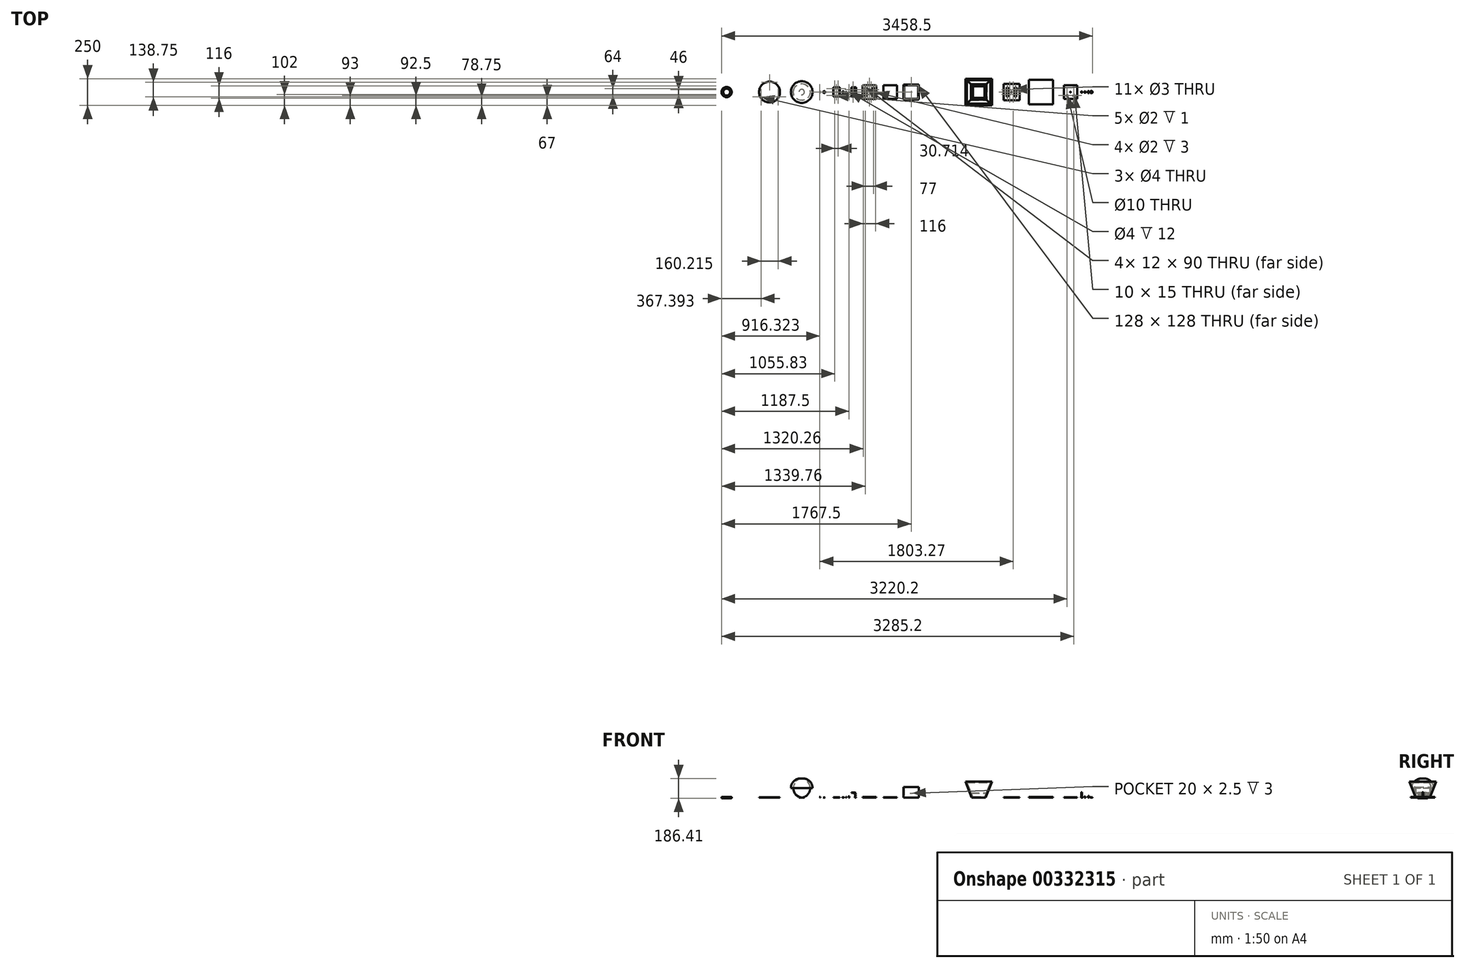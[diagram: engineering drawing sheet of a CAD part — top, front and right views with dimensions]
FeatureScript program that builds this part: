
annotation { "Feature Type Name" : "Feature", "Feature Type Description" : "" }
export const myFeature = defineFeature(function(context is Context, id is Id, definition is map)
    precondition{}
    {
        {
            var Q0;
            Q0=qCreatedBy(makeId("Top.planeOp"),FACE);
            var sketch = newSketch(context, id + "F0", { "sketchPlane" : qUnion([Q0])});
            skLineSegment(sketch, "E0.bottom", {"start": v(-350, -70) * mm, "end": v(-210, -70) * mm});
            skLineSegment(sketch, "E0.top", {"start": v(-350, 70) * mm, "end": v(-210, 70) * mm});
            skLineSegment(sketch, "E0.left", {"start": v(-350, -70) * mm, "end": v(-350, 70) * mm});
            skLineSegment(sketch, "E0.right", {"start": v(-210, -70) * mm, "end": v(-210, 70) * mm});
            skPoint(sketch, "E0.middle", {"position": v(-280, 0) * mm});
            skLineSegment(sketch, "E1.bottom", {"start": v(-344, -64) * mm, "end": v(-216, -64) * mm});
            skLineSegment(sketch, "E1.top", {"start": v(-344, 64) * mm, "end": v(-216, 64) * mm});
            skLineSegment(sketch, "E1.left", {"start": v(-344, -64) * mm, "end": v(-344, 64) * mm});
            skLineSegment(sketch, "E1.right", {"start": v(-216, -64) * mm, "end": v(-216, 64) * mm});
            skSolve(sketch);
        }
        {
            var Q0;
            Q0 = qSketchRegion(id + "F0", true);
            extrude(context, id + "F1", {"entities" : qUnion([Q0]), "depth" : 100 * mm});
        }
        {
            var Q0;
            Q0=qCreatedBy(makeId("Top.planeOp"),FACE);
            var sketch = newSketch(context, id + "F2", { "sketchPlane" : qUnion([Q0])});
            skLineSegment(sketch, "E2.bottom", {"start": v(-539.54, -64) * mm, "end": v(-411.54, -64) * mm});
            skLineSegment(sketch, "E2.top", {"start": v(-539.54, 64) * mm, "end": v(-411.54, 64) * mm});
            skLineSegment(sketch, "E2.left", {"start": v(-539.54, -64) * mm, "end": v(-539.54, 64) * mm});
            skLineSegment(sketch, "E2.right", {"start": v(-411.54, -64) * mm, "end": v(-411.54, 64) * mm});
            skPoint(sketch, "E2.middle", {"position": v(-475.54, 0) * mm});
            skSolve(sketch);
        }
        {
            var Q0;
            Q0 = qSketchRegion(id + "F2", true);
            extrude(context, id + "F3", {"entities" : qUnion([Q0]), "depth" : 4 * mm});
        }
        {
            var Q0;
            Q0=qCreatedBy(makeId("Top.planeOp"),FACE);
            var sketch = newSketch(context, id + "F4", { "sketchPlane" : qUnion([Q0])});
            skLineSegment(sketch, "E3.bottom", {"start": v(-733.24, -64) * mm, "end": v(-605.24, -64) * mm});
            skLineSegment(sketch, "E3.top", {"start": v(-733.24, 64) * mm, "end": v(-605.24, 64) * mm});
            skLineSegment(sketch, "E3.left", {"start": v(-733.24, -64) * mm, "end": v(-733.24, 64) * mm});
            skLineSegment(sketch, "E3.right", {"start": v(-605.24, -64) * mm, "end": v(-605.24, 64) * mm});
            skPoint(sketch, "E3.middle", {"position": v(-669.24, 0) * mm});
            skSolve(sketch);
        }
        {
            var Q0;
            Q0 = qSketchRegion(id + "F4", true);
            extrude(context, id + "F5", {"entities" : qUnion([Q0]), "depth" : 6 * mm});
        }
        {
            var Q0;
            Q0=makeQuery(id+"F5.opExtrude","CAP_FACE",FACE,{"disambiguationData":[OSD([sQuery(id+"F4.wireOp",EDGE,"E3.bottom"),sQuery(id+"F4.wireOp",EDGE,"E3.top"),sQuery(id+"F4.wireOp",EDGE,"E3.left"),sQuery(id+"F4.wireOp",EDGE,"E3.right")])],"isStart":false});
            var sketch = newSketch(context, id + "F6", { "sketchPlane" : qUnion([Q0])});
            skLineSegment(sketch, "E4.bottom", {"start": v(-713.74, 45) * mm, "end": v(-701.74, 45) * mm});
            skLineSegment(sketch, "E4.top", {"start": v(-713.74, -45) * mm, "end": v(-701.74, -45) * mm});
            skLineSegment(sketch, "E4.left", {"start": v(-713.74, 45) * mm, "end": v(-713.74, -45) * mm});
            skLineSegment(sketch, "E4.right", {"start": v(-701.74, 45) * mm, "end": v(-701.74, -45) * mm});
            skLineSegment(sketch, "E5.bottom", {"start": v(-636.74, 45) * mm, "end": v(-624.74, 45) * mm});
            skLineSegment(sketch, "E5.top", {"start": v(-636.74, -45) * mm, "end": v(-624.74, -45) * mm});
            skLineSegment(sketch, "E5.left", {"start": v(-636.74, 45) * mm, "end": v(-636.74, -45) * mm});
            skLineSegment(sketch, "E5.right", {"start": v(-624.74, 45) * mm, "end": v(-624.74, -45) * mm});
            skSolve(sketch);
        }
        {
            var Q0;
            Q0 = qSketchRegion(id + "F6", true);
            extrude(context, id + "F7", {"entities" : qUnion([Q0]), "operationType" : NewBodyOperationType.REMOVE, "oppositeDirection" : true, "depth" : 6 * mm});
        }
        {
            var Q0;
            Q0=qCreatedBy(makeId("Front.planeOp"),FACE);
            var sketch = newSketch(context, id + "F8", { "sketchPlane" : qUnion([Q0])});
            skLineSegment(sketch, "E6", {"start": v(-794.34, 0) * mm, "end": v(-805.34, 0) * mm});
            skLineSegment(sketch, "E7", {"start": v(-805.34, 0) * mm, "end": v(-805.34, 2) * mm});
            skLineSegment(sketch, "E8", {"start": v(-805.34, 2) * mm, "end": v(-803.34, 2) * mm});
            skLineSegment(sketch, "E9", {"start": v(-803.34, 2) * mm, "end": v(-803.34, 4.5) * mm});
            skLineSegment(sketch, "E10", {"start": v(-803.34, 4.5) * mm, "end": v(-805.34, 4.5) * mm});
            skLineSegment(sketch, "E11", {"start": v(-805.34, 4.5) * mm, "end": v(-805.34, 5.5) * mm});
            skLineSegment(sketch, "E12", {"start": v(-805.34, 5.5) * mm, "end": v(-803.34, 5.5) * mm});
            skLineSegment(sketch, "E13", {"start": v(-803.34, 5.5) * mm, "end": v(-803.34, 8) * mm});
            skLineSegment(sketch, "E14", {"start": v(-803.34, 8) * mm, "end": v(-805.34, 8) * mm});
            skLineSegment(sketch, "E15", {"start": v(-805.34, 8) * mm, "end": v(-805.34, 9) * mm});
            skLineSegment(sketch, "E16", {"start": v(-805.34, 9) * mm, "end": v(-803.34, 9) * mm});
            skLineSegment(sketch, "E17", {"start": v(-803.34, 9) * mm, "end": v(-803.34, 11.5) * mm});
            skLineSegment(sketch, "E18", {"start": v(-803.34, 11.5) * mm, "end": v(-805.34, 11.5) * mm});
            skLineSegment(sketch, "E19", {"start": v(-805.34, 11.5) * mm, "end": v(-805.34, 12.5) * mm});
            skLineSegment(sketch, "E20", {"start": v(-805.34, 12.5) * mm, "end": v(-803.34, 12.5) * mm});
            skLineSegment(sketch, "E21", {"start": v(-803.34, 12.5) * mm, "end": v(-803.34, 15) * mm});
            skLineSegment(sketch, "E22", {"start": v(-803.34, 15) * mm, "end": v(-805.34, 15) * mm});
            skLineSegment(sketch, "E23", {"start": v(-805.34, 15) * mm, "end": v(-805.34, 16) * mm});
            skLineSegment(sketch, "E24", {"start": v(-805.34, 16) * mm, "end": v(-803.34, 16) * mm});
            skLineSegment(sketch, "E25", {"start": v(-803.34, 16) * mm, "end": v(-803.34, 18.5) * mm});
            skLineSegment(sketch, "E26", {"start": v(-803.34, 18.5) * mm, "end": v(-805.34, 18.5) * mm});
            skLineSegment(sketch, "E27", {"start": v(-805.34, 18.5) * mm, "end": v(-805.34, 19.5) * mm});
            skLineSegment(sketch, "E28", {"start": v(-805.34, 19.5) * mm, "end": v(-803.34, 19.5) * mm});
            skLineSegment(sketch, "E29", {"start": v(-803.34, 19.5) * mm, "end": v(-803.34, 22) * mm});
            skLineSegment(sketch, "E30", {"start": v(-803.34, 22) * mm, "end": v(-805.34, 22) * mm});
            skLineSegment(sketch, "E31", {"start": v(-805.34, 22) * mm, "end": v(-805.34, 23) * mm});
            skLineSegment(sketch, "E32", {"start": v(-805.34, 23) * mm, "end": v(-803.34, 23) * mm});
            skLineSegment(sketch, "E33", {"start": v(-803.34, 23) * mm, "end": v(-803.34, 25.5) * mm});
            skLineSegment(sketch, "E34", {"start": v(-803.34, 25.5) * mm, "end": v(-805.34, 25.5) * mm});
            skLineSegment(sketch, "E35", {"start": v(-805.34, 25.5) * mm, "end": v(-805.34, 26.5) * mm});
            skLineSegment(sketch, "E36", {"start": v(-805.34, 26.5) * mm, "end": v(-803.34, 26.5) * mm});
            skLineSegment(sketch, "E37", {"start": v(-803.34, 26.5) * mm, "end": v(-803.34, 29) * mm});
            skLineSegment(sketch, "E38", {"start": v(-803.34, 29) * mm, "end": v(-805.34, 29) * mm});
            skLineSegment(sketch, "E39", {"start": v(-805.34, 29) * mm, "end": v(-805.34, 30) * mm});
            skLineSegment(sketch, "E40", {"start": v(-805.34, 30) * mm, "end": v(-803.34, 30) * mm});
            skLineSegment(sketch, "E41", {"start": v(-803.34, 30) * mm, "end": v(-803.34, 32.5) * mm});
            skLineSegment(sketch, "E42", {"start": v(-803.34, 32.5) * mm, "end": v(-809.34, 32.5) * mm});
            skLineSegment(sketch, "E43", {"start": v(-809.34, 32.5) * mm, "end": v(-809.34, 34) * mm});
            skLineSegment(sketch, "E44", {"start": v(-809.34, 34) * mm, "end": v(-803.34, 34) * mm});
            skLineSegment(sketch, "E45", {"start": v(-803.34, 34) * mm, "end": v(-803.34, 36.5) * mm});
            skLineSegment(sketch, "E46", {"start": v(-803.34, 36.5) * mm, "end": v(-809.34, 36.5) * mm});
            skLineSegment(sketch, "E47", {"start": v(-809.34, 36.5) * mm, "end": v(-809.34, 38) * mm});
            skLineSegment(sketch, "E48", {"start": v(-809.34, 38) * mm, "end": v(-803.34, 38) * mm});
            skLineSegment(sketch, "E49", {"start": v(-803.34, 38) * mm, "end": v(-803.34, 40.5) * mm});
            skLineSegment(sketch, "E50", {"start": v(-803.34, 40.5) * mm, "end": v(-809.34, 40.5) * mm});
            skLineSegment(sketch, "E51", {"start": v(-809.34, 40.5) * mm, "end": v(-809.34, 42) * mm});
            skLineSegment(sketch, "E52", {"start": v(-809.34, 42) * mm, "end": v(-803.34, 42) * mm});
            skLineSegment(sketch, "E53", {"start": v(-803.34, 42) * mm, "end": v(-803.34, 44.5) * mm});
            skLineSegment(sketch, "E54", {"start": v(-803.34, 44.5) * mm, "end": v(-836.34, 44.5) * mm});
            skLineSegment(sketch, "E55", {"start": v(-836.34, 44.5) * mm, "end": v(-836.34, 49) * mm});
            skLineSegment(sketch, "E56", {"start": v(-836.34, 49) * mm, "end": v(-808.34, 49) * mm});
            skLineSegment(sketch, "E57", {"start": v(-808.34, 49) * mm, "end": v(-808.34, 50) * mm});
            skLineSegment(sketch, "E58", {"start": v(-808.34, 50) * mm, "end": v(-807.34, 50) * mm});
            skLineSegment(sketch, "E59", {"start": v(-807.34, 50) * mm, "end": v(-807.34, 49) * mm});
            skLineSegment(sketch, "E60", {"start": v(-807.34, 49) * mm, "end": v(-805.34, 49) * mm});
            skLineSegment(sketch, "E61", {"start": v(-805.34, 49) * mm, "end": v(-805.34, 50) * mm});
            skLineSegment(sketch, "E62", {"start": v(-805.34, 50) * mm, "end": v(-804.34, 50) * mm});
            skLineSegment(sketch, "E63", {"start": v(-804.34, 50) * mm, "end": v(-804.34, 49) * mm});
            skLineSegment(sketch, "E64", {"start": v(-804.34, 49) * mm, "end": v(-802.34, 49) * mm});
            skLineSegment(sketch, "E65", {"start": v(-802.34, 49) * mm, "end": v(-802.34, 50) * mm});
            skLineSegment(sketch, "E66", {"start": v(-802.34, 50) * mm, "end": v(-801.34, 50) * mm});
            skLineSegment(sketch, "E67", {"start": v(-801.34, 50) * mm, "end": v(-801.34, 46) * mm});
            skLineSegment(sketch, "E68", {"start": v(-801.34, 46) * mm, "end": v(-795.34, 46) * mm});
            skLineSegment(sketch, "E69", {"start": v(-795.34, 46) * mm, "end": v(-795.34, 44.5) * mm});
            skLineSegment(sketch, "E70", {"start": v(-795.34, 44.5) * mm, "end": v(-801.34, 44.5) * mm});
            skLineSegment(sketch, "E71", {"start": v(-801.34, 44.5) * mm, "end": v(-801.34, 42) * mm});
            skLineSegment(sketch, "E72", {"start": v(-801.34, 42) * mm, "end": v(-795.34, 42) * mm});
            skLineSegment(sketch, "E73", {"start": v(-795.34, 42) * mm, "end": v(-795.34, 40.5) * mm});
            skLineSegment(sketch, "E74", {"start": v(-795.34, 40.5) * mm, "end": v(-801.34, 40.5) * mm});
            skLineSegment(sketch, "E75", {"start": v(-801.34, 40.5) * mm, "end": v(-801.34, 38) * mm});
            skLineSegment(sketch, "E76", {"start": v(-801.34, 38) * mm, "end": v(-795.34, 38) * mm});
            skLineSegment(sketch, "E77", {"start": v(-795.34, 38) * mm, "end": v(-795.34, 36.5) * mm});
            skLineSegment(sketch, "E78", {"start": v(-795.34, 36.5) * mm, "end": v(-801.34, 36.5) * mm});
            skLineSegment(sketch, "E79", {"start": v(-801.34, 36.5) * mm, "end": v(-801.34, 34) * mm});
            skLineSegment(sketch, "E80", {"start": v(-801.34, 34) * mm, "end": v(-795.34, 34) * mm});
            skLineSegment(sketch, "E81", {"start": v(-795.34, 34) * mm, "end": v(-795.34, 32.5) * mm});
            skLineSegment(sketch, "E82", {"start": v(-795.34, 32.5) * mm, "end": v(-801.34, 32.5) * mm});
            skLineSegment(sketch, "E83", {"start": v(-801.34, 32.5) * mm, "end": v(-801.34, 30) * mm});
            skLineSegment(sketch, "E84", {"start": v(-801.34, 30) * mm, "end": v(-795.34, 30) * mm});
            skLineSegment(sketch, "E85", {"start": v(-795.34, 30) * mm, "end": v(-795.34, 28.5) * mm});
            skLineSegment(sketch, "E86", {"start": v(-795.34, 28.5) * mm, "end": v(-801.34, 28.5) * mm});
            skLineSegment(sketch, "E87", {"start": v(-801.34, 28.5) * mm, "end": v(-801.34, 26) * mm});
            skLineSegment(sketch, "E88", {"start": v(-801.34, 26) * mm, "end": v(-795.34, 26) * mm});
            skLineSegment(sketch, "E89", {"start": v(-795.34, 26) * mm, "end": v(-795.34, 24.5) * mm});
            skLineSegment(sketch, "E90", {"start": v(-795.34, 24.5) * mm, "end": v(-801.34, 24.5) * mm});
            skLineSegment(sketch, "E91", {"start": v(-801.34, 24.5) * mm, "end": v(-801.34, 22) * mm});
            skLineSegment(sketch, "E92", {"start": v(-801.34, 22) * mm, "end": v(-795.34, 22) * mm});
            skLineSegment(sketch, "E93", {"start": v(-795.34, 22) * mm, "end": v(-795.34, 20.5) * mm});
            skLineSegment(sketch, "E94", {"start": v(-795.34, 20.5) * mm, "end": v(-801.34, 20.5) * mm});
            skLineSegment(sketch, "E95", {"start": v(-801.34, 20.5) * mm, "end": v(-801.34, 18) * mm});
            skLineSegment(sketch, "E96", {"start": v(-801.34, 18) * mm, "end": v(-795.34, 18) * mm});
            skLineSegment(sketch, "E97", {"start": v(-795.34, 18) * mm, "end": v(-795.34, 16.5) * mm});
            skLineSegment(sketch, "E98", {"start": v(-795.34, 16.5) * mm, "end": v(-801.34, 16.5) * mm});
            skLineSegment(sketch, "E99", {"start": v(-801.34, 16.5) * mm, "end": v(-801.34, 14) * mm});
            skLineSegment(sketch, "E100", {"start": v(-801.34, 14) * mm, "end": v(-795.34, 14) * mm});
            skLineSegment(sketch, "E101", {"start": v(-795.34, 14) * mm, "end": v(-795.34, 12.5) * mm});
            skLineSegment(sketch, "E102", {"start": v(-795.34, 12.5) * mm, "end": v(-801.34, 12.5) * mm});
            skLineSegment(sketch, "E103", {"start": v(-801.34, 12.5) * mm, "end": v(-801.34, 10) * mm});
            skLineSegment(sketch, "E104", {"start": v(-801.34, 10) * mm, "end": v(-795.34, 10) * mm});
            skLineSegment(sketch, "E105", {"start": v(-795.34, 10) * mm, "end": v(-795.34, 8.5) * mm});
            skLineSegment(sketch, "E106", {"start": v(-795.34, 8.5) * mm, "end": v(-801.34, 8.5) * mm});
            skLineSegment(sketch, "E107", {"start": v(-801.34, 8.5) * mm, "end": v(-801.34, 6) * mm});
            skLineSegment(sketch, "E108", {"start": v(-801.34, 6) * mm, "end": v(-795.34, 6) * mm});
            skLineSegment(sketch, "E109", {"start": v(-795.34, 6) * mm, "end": v(-795.34, 4.5) * mm});
            skLineSegment(sketch, "E110", {"start": v(-795.34, 4.5) * mm, "end": v(-801.34, 4.5) * mm});
            skLineSegment(sketch, "E111", {"start": v(-801.34, 4.5) * mm, "end": v(-801.34, 2) * mm});
            skLineSegment(sketch, "E112", {"start": v(-801.34, 2) * mm, "end": v(-794.34, 2) * mm});
            skLineSegment(sketch, "E113", {"start": v(-794.34, 2) * mm, "end": v(-794.34, 0) * mm});
            skSolve(sketch);
        }
        {
            var Q0;
            Q0 = qSketchRegion(id + "F8", true);
            extrude(context, id + "F9", {"entities" : qUnion([Q0]), "endBound" : BoundingType.SYMMETRIC, "depth" : 86 * mm});
        }
        {
            var Q0;
            Q0=makeQuery(id+"F9.opExtrude","SWEPT_FACE",FACE,{"disambiguationData":[OSD([sQuery(id+"F8.wireOp",EDGE,"E56")])]});
            var sketch = newSketch(context, id + "F10", { "sketchPlane" : qUnion([Q0])});
            skCircle(sketch, "E114", {"center": v(-822.34, 23) * mm, "radius": 1.5 * mm});
            skPoint(sketch, "E114.centerSnap0", {"position": v(-822.34, 43) * mm});
            skCircle(sketch, "E115", {"center": v(-822.34, -23) * mm, "radius": 1.5 * mm});
            skPoint(sketch, "E115.centerSnap0", {"position": v(-822.34, -43) * mm});
            skSolve(sketch);
        }
        {
            var Q0;
            Q0 = qSketchRegion(id + "F10", true);
            extrude(context, id + "F11", {"entities" : qUnion([Q0]), "operationType" : NewBodyOperationType.REMOVE, "oppositeDirection" : true, "depth" : 5 * mm});
        }
        {
            var Q0;
            Q0=makeQuery(id+"F5.opExtrude","CAP_FACE",FACE,{"disambiguationData":[OSD([sQuery(id+"F4.wireOp",EDGE,"E3.bottom"),sQuery(id+"F4.wireOp",EDGE,"E3.top"),sQuery(id+"F4.wireOp",EDGE,"E3.left"),sQuery(id+"F4.wireOp",EDGE,"E3.right")])],"isStart":false});
            var sketch = newSketch(context, id + "F12", { "sketchPlane" : qUnion([Q0])});
            skCircle(sketch, "E116", {"center": v(-652.74, 23) * mm, "radius": 1.5 * mm});
            skCircle(sketch, "E117", {"center": v(-652.74, -23) * mm, "radius": 1.5 * mm});
            skCircle(sketch, "E118", {"center": v(-685.74, 23) * mm, "radius": 1.5 * mm});
            skCircle(sketch, "E119", {"center": v(-685.74, -23) * mm, "radius": 1.5 * mm});
            skSolve(sketch);
        }
        {
            var Q0;
            Q0 = qSketchRegion(id + "F12", true);
            extrude(context, id + "F13", {"entities" : qUnion([Q0]), "operationType" : NewBodyOperationType.REMOVE, "oppositeDirection" : true, "depth" : 6 * mm});
        }
        {
            var Q0;
            Q0=qCreatedBy(makeId("Top.planeOp"),FACE);
            var sketch = newSketch(context, id + "F14", { "sketchPlane" : qUnion([Q0])});
            skCircle(sketch, "E120", {"center": v(-860, 0) * mm, "radius": 3 * mm});
            skCircle(sketch, "E121", {"center": v(-860, 0) * mm, "radius": 2 * mm});
            skSolve(sketch);
        }
        {
            var Q0;
            Q0 = qSketchRegion(id + "F14", true);
            extrude(context, id + "F15", {"entities" : qUnion([Q0]), "depth" : 12 * mm});
        }
        {
            var Q0;
            Q0=qCreatedBy(makeId("Top.planeOp"),FACE);
            var sketch = newSketch(context, id + "F16", { "sketchPlane" : qUnion([Q0])});
            skLineSegment(sketch, "E122.bottom", {"start": v(-1006.28, -43) * mm, "end": v(-945.28, -43) * mm});
            skLineSegment(sketch, "E122.top", {"start": v(-1006.28, 43) * mm, "end": v(-945.28, 43) * mm});
            skLineSegment(sketch, "E122.left", {"start": v(-1006.28, -43) * mm, "end": v(-1006.28, 43) * mm});
            skLineSegment(sketch, "E122.right", {"start": v(-945.28, -43) * mm, "end": v(-945.28, 43) * mm});
            skPoint(sketch, "E122.middle", {"position": v(-975.78, 0) * mm});
            skSolve(sketch);
        }
        {
            var Q0;
            Q0 = qSketchRegion(id + "F16", true);
            extrude(context, id + "F17", {"entities" : qUnion([Q0]), "depth" : 2 * mm});
        }
        {
            var Q0;
            Q0=qCreatedBy(makeId("Top.planeOp"),FACE);
            var sketch = newSketch(context, id + "F18", { "sketchPlane" : qUnion([Q0])});
            skLineSegment(sketch, "E123", {"start": v(-1085, 8.66) * mm, "end": v(-1080, 0) * mm});
            skLineSegment(sketch, "E124", {"start": v(-1080, 0) * mm, "end": v(-1085, -8.66) * mm});
            skLineSegment(sketch, "E125", {"start": v(-1085, -8.66) * mm, "end": v(-1095, -8.66) * mm});
            skLineSegment(sketch, "E126", {"start": v(-1095, -8.66) * mm, "end": v(-1100, 0) * mm});
            skLineSegment(sketch, "E127", {"start": v(-1100, 0) * mm, "end": v(-1095, 8.66) * mm});
            skLineSegment(sketch, "E128", {"start": v(-1095, 8.66) * mm, "end": v(-1085, 8.66) * mm});
            skSolve(sketch);
        }
        {
            var Q0;
            Q0 = qSketchRegion(id + "F18", true);
            extrude(context, id + "F19", {"entities" : qUnion([Q0]), "depth" : 1.5 * mm});
        }
        {
            var Q0;
            Q0=makeQuery(id+"F19.opExtrude","CAP_FACE",FACE,{"disambiguationData":[OSD([sQuery(id+"F18.wireOp",EDGE,"E123"),sQuery(id+"F18.wireOp",EDGE,"E124"),sQuery(id+"F18.wireOp",EDGE,"E125"),sQuery(id+"F18.wireOp",EDGE,"E126"),sQuery(id+"F18.wireOp",EDGE,"E127"),sQuery(id+"F18.wireOp",EDGE,"E128")])],"isStart":false});
            var sketch = newSketch(context, id + "F20", { "sketchPlane" : qUnion([Q0])});
            skLineSegment(sketch, "E129.bottom", {"start": v(-1092.5, -3.5) * mm, "end": v(-1087.5, -3.5) * mm});
            skLineSegment(sketch, "E129.top", {"start": v(-1092.5, 3.5) * mm, "end": v(-1087.5, 3.5) * mm});
            skLineSegment(sketch, "E129.left", {"start": v(-1092.5, -3.5) * mm, "end": v(-1092.5, 3.5) * mm});
            skLineSegment(sketch, "E129.right", {"start": v(-1087.5, -3.5) * mm, "end": v(-1087.5, 3.5) * mm});
            skPoint(sketch, "E129.middle", {"position": v(-1090, 0) * mm});
            skPoint(sketch, "E129.middle.positionSnap0", {"position": v(-1090, 8.66) * mm});
            skPoint(sketch, "E129.centerSnap0", {"position": v(-1090, 8.66) * mm});
            skSolve(sketch);
        }
        {
            var Q0;
            Q0 = qSketchRegion(id + "F20", true);
            extrude(context, id + "F21", {"entities" : qUnion([Q0]), "operationType" : NewBodyOperationType.ADD, "depth" : 1 * mm});
        }
        {
            var Q0;
            Q0=makeQuery(id+"F21.opExtrude","CAP_FACE",FACE,{"disambiguationData":[OSD([sQuery(id+"F20.wireOp",EDGE,"E129.bottom"),sQuery(id+"F20.wireOp",EDGE,"E129.top"),sQuery(id+"F20.wireOp",EDGE,"E129.left"),sQuery(id+"F20.wireOp",EDGE,"E129.right")])],"isStart":false});
            var sketch = newSketch(context, id + "F22", { "sketchPlane" : qUnion([Q0])});
            skCircle(sketch, "E130", {"center": v(-1090, 0) * mm, "radius": 1.5 * mm});
            skPoint(sketch, "E130.centerSnap0", {"position": v(-1090, 3.5) * mm});
            skSolve(sketch);
        }
        {
            var Q0;
            Q0 = qSketchRegion(id + "F22", true);
            extrude(context, id + "F23", {"entities" : qUnion([Q0]), "operationType" : NewBodyOperationType.ADD, "depth" : 2 * mm});
        }
        {
            var Q0;
            Q0=makeQuery(id+"F23.opExtrude","CAP_EDGE",EDGE,{"disambiguationData":[OSD([sQuery(id+"F22.wireOp",EDGE,"E130")])],"isStart":false});
            fillet(context, id + "F24", {"entities" : qUnion([Q0]), "radius" : 1.5 * mm, "tangentPropagation" : true, "allowEdgeOverflow" : false});
        }
        {
            var Q0;
            Q0=makeQuery(id+"F17.opExtrude","CAP_FACE",FACE,{"disambiguationData":[OSD([sQuery(id+"F16.wireOp",EDGE,"E122.bottom"),sQuery(id+"F16.wireOp",EDGE,"E122.top"),sQuery(id+"F16.wireOp",EDGE,"E122.left"),sQuery(id+"F16.wireOp",EDGE,"E122.right")])],"isStart":false});
            var sketch = newSketch(context, id + "F25", { "sketchPlane" : qUnion([Q0])});
            skCircle(sketch, "E131", {"center": v(-991.67, 32) * mm, "radius": 1 * mm});
            skCircle(sketch, "E132", {"center": v(-960.96, 32) * mm, "radius": 1 * mm});
            skPoint(sketch, "E133.centerSnap0", {"position": v(-1006.28, 0) * mm});
            skCircle(sketch, "E134", {"center": v(-960.96, -32) * mm, "radius": 1 * mm});
            skCircle(sketch, "E135", {"center": v(-991.67, -32) * mm, "radius": 1 * mm});
            skCircle(sketch, "E136", {"center": v(-975.78, 0) * mm, "radius": 1 * mm});
            skPoint(sketch, "E136.centerSnap0", {"position": v(-975.78, 43) * mm});
            skSolve(sketch);
        }
        {
            var Q0;
            Q0 = qSketchRegion(id + "F25", true);
            extrude(context, id + "F26", {"entities" : qUnion([Q0]), "operationType" : NewBodyOperationType.REMOVE, "oppositeDirection" : true, "depth" : 1 * mm});
        }
        {
            var Q0;
            Q0=qCreatedBy(makeId("Top.planeOp"),FACE);
            var sketch = newSketch(context, id + "F27", { "sketchPlane" : qUnion([Q0])});
            skCircle(sketch, "E137", {"center": v(-914.38, 0) * mm, "radius": 7.5 * mm});
            skSolve(sketch);
        }
        {
            var Q0;
            Q0 = qSketchRegion(id + "F27", true);
            extrude(context, id + "F28", {"entities" : qUnion([Q0]), "depth" : 2 * mm});
        }
        {
            var Q0;
            Q0=makeQuery(id+"F28.opExtrude","CAP_FACE",FACE,{"disambiguationData":[OSD([sQuery(id+"F27.wireOp",EDGE,"E137")])],"isStart":false});
            var sketch = newSketch(context, id + "F29", { "sketchPlane" : qUnion([Q0])});
            skCircle(sketch, "E138", {"center": v(-912.88, 0) * mm, "radius": 1 * mm});
            skSolve(sketch);
        }
        {
            var Q0;
            Q0 = qSketchRegion(id + "F29", true);
            extrude(context, id + "F30", {"entities" : qUnion([Q0]), "operationType" : NewBodyOperationType.REMOVE, "oppositeDirection" : true, "depth" : 2 * mm});
        }
        {
            var Q0;
            Q0=qCreatedBy(makeId("Front.planeOp"),FACE);
            var sketch = newSketch(context, id + "F31", { "sketchPlane" : qUnion([Q0])});
            skLineSegment(sketch, "E139", {"start": v(-884, 0) * mm, "end": v(-884, 4) * mm});
            skLineSegment(sketch, "E140", {"start": v(-884, 4) * mm, "end": v(-883, 4) * mm});
            skLineSegment(sketch, "E141", {"start": v(-883, 4) * mm, "end": v(-883, 5) * mm});
            skLineSegment(sketch, "E142", {"start": v(-883, 5) * mm, "end": v(-885, 5) * mm});
            skLineSegment(sketch, "E143", {"start": v(-885, 5) * mm, "end": v(-885, 0) * mm});
            skLineSegment(sketch, "E144", {"start": v(-885, 0) * mm, "end": v(-884, 0) * mm});
            skSolve(sketch);
        }
        {
            var Q0;
            Q0=qCreatedBy(makeId("Front.planeOp"),FACE);
            var sketch = newSketch(context, id + "F32", { "sketchPlane" : qUnion([Q0])});
            skLineSegment(sketch, "E145", {"start": v(-885, 6.98) * mm, "end": v(-885, -1.02) * mm, "construction": true});
            skSolve(sketch);
        }
        {
            var Q0;
            Q0=makeQuery(id+"F31.imprint","IMPRINT",FACE,{"disambiguationData":[TD([[makeQuery(id+"F31.imprint","IMPRINT",EDGE,{"derivedFrom":sQuery(id+"F31.wireOp",EDGE,"E139")}),1.0]])]});
            var Q1;
            Q1=sQuery(id+"F32.wireOp",EDGE,"E145");
            var Q2;
            Q2=sQuery(id+"F32.wireOp",EDGE,"E145");
            revolve(context, id + "F33", {"entities" : qUnion([Q0]), "surfaceEntities" : qUnion([Q1]), "axis" : qUnion([Q2]), "revolveType" : RevolveType.FULL});
        }
        {
            var Q0;
            Q0=makeQuery(id+"F5.opExtrude","CAP_FACE",FACE,{"disambiguationData":[OSD([sQuery(id+"F4.wireOp",EDGE,"E3.bottom"),sQuery(id+"F4.wireOp",EDGE,"E3.top"),sQuery(id+"F4.wireOp",EDGE,"E3.left"),sQuery(id+"F4.wireOp",EDGE,"E3.right")])],"isStart":true});
            var sketch = newSketch(context, id + "F34", { "sketchPlane" : qUnion([Q0])});
            skCircle(sketch, "E146", {"center": v(-669.24, 58) * mm, "radius": 1 * mm});
            skPoint(sketch, "E146.centerSnap0", {"position": v(-669.24, 64) * mm});
            skCircle(sketch, "E147", {"center": v(-669.24, -58) * mm, "radius": 1 * mm});
            skPoint(sketch, "E147.centerSnap0", {"position": v(-669.24, -64) * mm});
            skCircle(sketch, "E148", {"center": v(-727.24, 0) * mm, "radius": 1 * mm});
            skPoint(sketch, "E148.centerSnap0", {"position": v(-733.24, 0) * mm});
            skCircle(sketch, "E149", {"center": v(-611.24, 0) * mm, "radius": 1 * mm});
            skPoint(sketch, "E149.centerSnap0", {"position": v(-605.24, 0) * mm});
            skSolve(sketch);
        }
        {
            var Q0;
            Q0 = qSketchRegion(id + "F34", true);
            extrude(context, id + "F35", {"entities" : qUnion([Q0]), "operationType" : NewBodyOperationType.REMOVE, "oppositeDirection" : true, "depth" : 3 * mm});
        }
        {
            var Q0;
            Q0=makeQuery(id+"F1.opExtrude","SWEPT_FACE",FACE,{"disambiguationData":[OSD([sQuery(id+"F0.wireOp",EDGE,"E1.top")])]});
            var sketch = newSketch(context, id + "F36", { "sketchPlane" : qUnion([Q0])});
            skLineSegment(sketch, "E150.bottom", {"start": v(-290, 40) * mm, "end": v(-270, 40) * mm});
            skLineSegment(sketch, "E150.top", {"start": v(-290, 42.5) * mm, "end": v(-270, 42.5) * mm});
            skLineSegment(sketch, "E150.left", {"start": v(-290, 40) * mm, "end": v(-290, 42.5) * mm});
            skLineSegment(sketch, "E150.right", {"start": v(-270, 40) * mm, "end": v(-270, 42.5) * mm});
            skPoint(sketch, "E150.middle", {"position": v(-280, 41.25) * mm});
            skPoint(sketch, "E150.middle.positionSnap0", {"position": v(-280, 0) * mm});
            skPoint(sketch, "E150.centerSnap0", {"position": v(-280, 0) * mm});
            skSolve(sketch);
        }
        {
            var Q0;
            Q0 = qSketchRegion(id + "F36", true);
            extrude(context, id + "F37", {"entities" : qUnion([Q0]), "operationType" : NewBodyOperationType.REMOVE, "oppositeDirection" : true, "depth" : 3 * mm});
        }
        {
            var Q0;
            Q0=qCreatedBy(makeId("Front.planeOp"),FACE);
            var sketch = newSketch(context, id + "F38", { "sketchPlane" : qUnion([Q0])});
            skLineSegment(sketch, "E151", {"start": v(-280, 126.9) * mm, "end": v(-280, -33.1) * mm, "construction": true});
            skSolve(sketch);
        }
        {
            var Q0;
            Q0=qCreatedBy(makeId("Top.planeOp"),FACE);
            var sketch = newSketch(context, id + "F39", { "sketchPlane" : qUnion([Q0])});
            skLineSegment(sketch, "E152.bottom", {"start": v(225, -125) * mm, "end": v(475, -125) * mm});
            skLineSegment(sketch, "E152.top", {"start": v(225, 125) * mm, "end": v(475, 125) * mm});
            skLineSegment(sketch, "E152.left", {"start": v(225, -125) * mm, "end": v(225, 125) * mm});
            skLineSegment(sketch, "E152.right", {"start": v(475, -125) * mm, "end": v(475, 125) * mm});
            skPoint(sketch, "E152.middle", {"position": v(350, 0) * mm});
            skSolve(sketch);
        }
        {
            var Q0;
            Q0 = qSketchRegion(id + "F39", true);
            extrude(context, id + "F40", {"entities" : qUnion([Q0]), "depth" : 150 * mm});
        }
        {
            var Q0;
            Q0=makeQuery(id+"F40.opExtrude","SWEPT_FACE",FACE,{"disambiguationData":[OSD([sQuery(id+"F39.wireOp",EDGE,"E152.bottom")])]});
            var sketch = newSketch(context, id + "F41", { "sketchPlane" : qUnion([Q0])});
            skLineSegment(sketch, "E153", {"start": v(225, 150) * mm, "end": v(225, 0) * mm});
            skLineSegment(sketch, "E154", {"start": v(225, 0) * mm, "end": v(285, 0) * mm});
            skLineSegment(sketch, "E155", {"start": v(285, 0) * mm, "end": v(225, 150) * mm});
            skLineSegment(sketch, "E156", {"start": v(475, 150) * mm, "end": v(475, 0) * mm});
            skLineSegment(sketch, "E157", {"start": v(475, 0) * mm, "end": v(415, 0) * mm});
            skLineSegment(sketch, "E158", {"start": v(415, 0) * mm, "end": v(475, 150) * mm});
            skSolve(sketch);
        }
        {
            var Q0;
            Q0=makeQuery(id+"F40.opExtrude","SWEPT_FACE",FACE,{"disambiguationData":[OSD([sQuery(id+"F39.wireOp",EDGE,"E152.right")])]});
            var sketch = newSketch(context, id + "F42", { "sketchPlane" : qUnion([Q0])});
            skLineSegment(sketch, "E159", {"start": v(-125, 150) * mm, "end": v(-125, 0) * mm});
            skLineSegment(sketch, "E160", {"start": v(-125, 0) * mm, "end": v(-65, 0) * mm});
            skLineSegment(sketch, "E161", {"start": v(-65, 0) * mm, "end": v(-125, 150) * mm});
            skLineSegment(sketch, "E162", {"start": v(125, 150) * mm, "end": v(125, 0) * mm});
            skLineSegment(sketch, "E163", {"start": v(125, 0) * mm, "end": v(65, 0) * mm});
            skLineSegment(sketch, "E164", {"start": v(65, 0) * mm, "end": v(125, 150) * mm});
            skSolve(sketch);
        }
        {
            var Q0;
            Q0 = qSketchRegion(id + "F41", true);
            extrude(context, id + "F43", {"entities" : qUnion([Q0]), "operationType" : NewBodyOperationType.REMOVE, "oppositeDirection" : true, "depth" : 250 * mm});
        }
        {
            var Q0;
            Q0 = qSketchRegion(id + "F42", true);
            extrude(context, id + "F44", {"entities" : qUnion([Q0]), "operationType" : NewBodyOperationType.REMOVE, "oppositeDirection" : true, "depth" : 250 * mm});
        }
        {
            var Q0;
            Q0=qCreatedBy(makeId("Front.planeOp"),FACE);
            var sketch = newSketch(context, id + "F45", { "sketchPlane" : qUnion([Q0])});
            skLineSegment(sketch, "E165.bottom", {"start": v(235, 141) * mm, "end": v(465, 141) * mm});
            skLineSegment(sketch, "E165.top", {"start": v(235, 147) * mm, "end": v(465, 147) * mm});
            skLineSegment(sketch, "E165.left", {"start": v(235, 141) * mm, "end": v(235, 147) * mm});
            skLineSegment(sketch, "E165.right", {"start": v(465, 141) * mm, "end": v(465, 147) * mm});
            skPoint(sketch, "E165.middle", {"position": v(350, 144) * mm});
            skSolve(sketch);
        }
        {
            var Q0;
            Q0 = qSketchRegion(id + "F45", true);
            extrude(context, id + "F46", {"entities" : qUnion([Q0]), "operationType" : NewBodyOperationType.REMOVE, "endBound" : BoundingType.SYMMETRIC, "oppositeDirection" : true, "depth" : 230 * mm, "hasSecondDirection" : true, "secondDirectionOppositeDirection" : false, "secondDirectionDepth" : 25 * mm});
        }
        {
            var Q0;
            Q0=qCreatedBy(makeId("Front.planeOp"),FACE);
            var sketch = newSketch(context, id + "F47", { "sketchPlane" : qUnion([Q0])});
            skLineSegment(sketch, "E166.bottom", {"start": v(275, 42) * mm, "end": v(425, 42) * mm});
            skLineSegment(sketch, "E166.top", {"start": v(275, 46) * mm, "end": v(425, 46) * mm});
            skLineSegment(sketch, "E166.left", {"start": v(275, 42) * mm, "end": v(275, 46) * mm});
            skLineSegment(sketch, "E166.right", {"start": v(425, 42) * mm, "end": v(425, 46) * mm});
            skPoint(sketch, "E166.middle", {"position": v(350, 44) * mm});
            skSolve(sketch);
        }
        {
            var Q0;
            Q0 = qSketchRegion(id + "F47", true);
            extrude(context, id + "F48", {"entities" : qUnion([Q0]), "operationType" : NewBodyOperationType.REMOVE, "endBound" : BoundingType.SYMMETRIC, "oppositeDirection" : true, "depth" : 150 * mm});
        }
        {
            var Q0;
            Q0=makeQuery(id+"F40.opExtrude","CAP_FACE",FACE,{"disambiguationData":[OSD([sQuery(id+"F39.wireOp",EDGE,"E152.bottom"),sQuery(id+"F39.wireOp",EDGE,"E152.top"),sQuery(id+"F39.wireOp",EDGE,"E152.left"),sQuery(id+"F39.wireOp",EDGE,"E152.right")])],"isStart":false});
            var sketch = newSketch(context, id + "F49", { "sketchPlane" : qUnion([Q0])});
            skLineSegment(sketch, "E167.bottom", {"start": v(237, -113) * mm, "end": v(463, -113) * mm});
            skLineSegment(sketch, "E167.top", {"start": v(237, 113) * mm, "end": v(463, 113) * mm});
            skLineSegment(sketch, "E167.left", {"start": v(237, -113) * mm, "end": v(237, 113) * mm});
            skLineSegment(sketch, "E167.right", {"start": v(463, -113) * mm, "end": v(463, 113) * mm});
            skPoint(sketch, "E167.middle", {"position": v(350, 0) * mm});
            skPoint(sketch, "E167.middle.positionSnap0", {"position": v(350, 125) * mm});
            skPoint(sketch, "E167.centerSnap0", {"position": v(350, 125) * mm});
            skSolve(sketch);
        }
        {
            var Q0;
            Q0=makeQuery(id+"F40.opExtrude","CAP_FACE",FACE,{"disambiguationData":[OSD([sQuery(id+"F39.wireOp",EDGE,"E152.bottom"),sQuery(id+"F39.wireOp",EDGE,"E152.top"),sQuery(id+"F39.wireOp",EDGE,"E152.left"),sQuery(id+"F39.wireOp",EDGE,"E152.right")])],"isStart":true});
            var sketch = newSketch(context, id + "F50", { "sketchPlane" : qUnion([Q0])});
            skLineSegment(sketch, "E168.bottom", {"start": v(297, -53) * mm, "end": v(403, -53) * mm});
            skLineSegment(sketch, "E168.top", {"start": v(297, 53) * mm, "end": v(403, 53) * mm});
            skLineSegment(sketch, "E168.left", {"start": v(297, -53) * mm, "end": v(297, 53) * mm});
            skLineSegment(sketch, "E168.right", {"start": v(403, -53) * mm, "end": v(403, 53) * mm});
            skPoint(sketch, "E168.middle", {"position": v(350, 0) * mm});
            skPoint(sketch, "E168.middle.positionSnap0", {"position": v(350, 65) * mm});
            skPoint(sketch, "E168.centerSnap0", {"position": v(350, 65) * mm});
            skSolve(sketch);
        }
        {
            var Q0;
            Q0=qCreatedBy(makeId("Front.planeOp"),FACE);
            var sketch = newSketch(context, id + "F51", { "sketchPlane" : qUnion([Q0])});
            skLineSegment(sketch, "E169.bottom", {"start": v(287.5, 8) * mm, "end": v(412.5, 8) * mm});
            skLineSegment(sketch, "E169.top", {"start": v(287.5, 4) * mm, "end": v(412.5, 4) * mm});
            skLineSegment(sketch, "E169.left", {"start": v(287.5, 8) * mm, "end": v(287.5, 4) * mm});
            skLineSegment(sketch, "E169.right", {"start": v(412.5, 8) * mm, "end": v(412.5, 4) * mm});
            skPoint(sketch, "E169.middle", {"position": v(350, 6) * mm});
            skSolve(sketch);
        }
        {
            var Q0;
            Q0 = qSketchRegion(id + "F51", true);
            extrude(context, id + "F52", {"entities" : qUnion([Q0]), "operationType" : NewBodyOperationType.REMOVE, "endBound" : BoundingType.SYMMETRIC, "oppositeDirection" : true, "depth" : 125 * mm});
        }
        {
            var Q1;
            Q1 = qSketchRegion(id + "F49", true);
            var Q2;
            Q2 = qSketchRegion(id + "F50", true);
            loft(context, id + "F53", {"operationType" : NewBodyOperationType.REMOVE, "sheetProfilesArray" : [{ "sheetProfileEntities" : qUnion([Q1]) }, { "sheetProfileEntities" : qUnion([Q2]) }]});
        }
        {
            var Q0;
            Q0=makeQuery(id+"F40.opExtrude","CAP_FACE",FACE,{"disambiguationData":[OSD([sQuery(id+"F39.wireOp",EDGE,"E152.bottom"),sQuery(id+"F39.wireOp",EDGE,"E152.top"),sQuery(id+"F39.wireOp",EDGE,"E152.left"),sQuery(id+"F39.wireOp",EDGE,"E152.right")])],"isStart":false});
            var sketch = newSketch(context, id + "F54", { "sketchPlane" : qUnion([Q0])});
            skLineSegment(sketch, "E170", {"start": v(225, 124.95) * mm, "end": v(225.05, 125) * mm});
            skLineSegment(sketch, "E171", {"start": v(474.95, 125) * mm, "end": v(475, 124.95) * mm});
            skLineSegment(sketch, "E172", {"start": v(475, -124.95) * mm, "end": v(474.95, -125) * mm});
            skLineSegment(sketch, "E173", {"start": v(225, -124.95) * mm, "end": v(225.05, -125) * mm});
            skLineSegment(sketch, "E174", {"start": v(225, -124.95) * mm, "end": v(474.95, 125) * mm});
            skLineSegment(sketch, "E175", {"start": v(475, 124.95) * mm, "end": v(225.05, -125) * mm});
            skLineSegment(sketch, "E176", {"start": v(474.95, -125) * mm, "end": v(225, 124.95) * mm});
            skLineSegment(sketch, "E177", {"start": v(225.05, 125) * mm, "end": v(475, -124.95) * mm});
            skSolve(sketch);
        }
        {
            var Q0;
            Q0 = qSketchRegion(id + "F54", true);
            extrude(context, id + "F55", {"entities" : qUnion([Q0]), "operationType" : NewBodyOperationType.REMOVE, "oppositeDirection" : true, "depth" : 150 * mm});
        }
        {
            var Q0;
            Q0=qCreatedBy(makeId("Top.planeOp"),FACE);
            var sketch = newSketch(context, id + "F56", { "sketchPlane" : qUnion([Q0])});
            skLineSegment(sketch, "E178.bottom", {"start": v(580.59, -75) * mm, "end": v(730.59, -75) * mm});
            skLineSegment(sketch, "E178.top", {"start": v(580.59, 75) * mm, "end": v(730.59, 75) * mm});
            skLineSegment(sketch, "E178.left", {"start": v(580.59, -75) * mm, "end": v(580.59, 75) * mm});
            skLineSegment(sketch, "E178.right", {"start": v(730.59, -75) * mm, "end": v(730.59, 75) * mm});
            skPoint(sketch, "E178.middle", {"position": v(655.59, 0) * mm});
            skSolve(sketch);
        }
        {
            var Q0;
            Q0 = qSketchRegion(id + "F56", true);
            extrude(context, id + "F57", {"entities" : qUnion([Q0]), "depth" : 4 * mm});
        }
        {
            var Q0;
            Q0=qCreatedBy(makeId("Top.planeOp"),FACE);
            var sketch = newSketch(context, id + "F58", { "sketchPlane" : qUnion([Q0])});
            skLineSegment(sketch, "E179.bottom", {"start": v(816.1, -113) * mm, "end": v(1042.1, -113) * mm});
            skLineSegment(sketch, "E179.top", {"start": v(816.1, 113) * mm, "end": v(1042.1, 113) * mm});
            skLineSegment(sketch, "E179.left", {"start": v(816.1, -113) * mm, "end": v(816.1, 113) * mm});
            skLineSegment(sketch, "E179.right", {"start": v(1042.1, -113) * mm, "end": v(1042.1, 113) * mm});
            skPoint(sketch, "E179.middle", {"position": v(929.1, 0) * mm});
            skSolve(sketch);
        }
        {
            var Q0;
            Q0 = qSketchRegion(id + "F58", true);
            extrude(context, id + "F59", {"entities" : qUnion([Q0]), "depth" : 6 * mm});
        }
        {
            var Q0;
            Q0=makeQuery(id+"F57.opExtrude","CAP_FACE",FACE,{"disambiguationData":[OSD([sQuery(id+"F56.wireOp",EDGE,"E178.bottom"),sQuery(id+"F56.wireOp",EDGE,"E178.top"),sQuery(id+"F56.wireOp",EDGE,"E178.left"),sQuery(id+"F56.wireOp",EDGE,"E178.right")])],"isStart":false});
            var sketch = newSketch(context, id + "F60", { "sketchPlane" : qUnion([Q0])});
            skLineSegment(sketch, "E180.bottom", {"start": v(611.09, 45) * mm, "end": v(623.09, 45) * mm});
            skLineSegment(sketch, "E180.top", {"start": v(611.09, -45) * mm, "end": v(623.09, -45) * mm});
            skLineSegment(sketch, "E180.left", {"start": v(611.09, 45) * mm, "end": v(611.09, -45) * mm});
            skLineSegment(sketch, "E180.right", {"start": v(623.09, 45) * mm, "end": v(623.09, -45) * mm});
            skLineSegment(sketch, "E181.bottom", {"start": v(688.09, 45) * mm, "end": v(700.09, 45) * mm});
            skLineSegment(sketch, "E181.top", {"start": v(688.09, -45) * mm, "end": v(700.09, -45) * mm});
            skLineSegment(sketch, "E181.left", {"start": v(688.09, 45) * mm, "end": v(688.09, -45) * mm});
            skLineSegment(sketch, "E181.right", {"start": v(700.09, 45) * mm, "end": v(700.09, -45) * mm});
            skSolve(sketch);
        }
        {
            var Q0;
            Q0 = qSketchRegion(id + "F60", true);
            extrude(context, id + "F61", {"entities" : qUnion([Q0]), "operationType" : NewBodyOperationType.REMOVE, "oppositeDirection" : true, "depth" : 4 * mm});
        }
        {
            var Q0;
            Q0=makeQuery(id+"F57.opExtrude","CAP_FACE",FACE,{"disambiguationData":[OSD([sQuery(id+"F56.wireOp",EDGE,"E178.bottom"),sQuery(id+"F56.wireOp",EDGE,"E178.top"),sQuery(id+"F56.wireOp",EDGE,"E178.left"),sQuery(id+"F56.wireOp",EDGE,"E178.right")])],"isStart":false});
            var sketch = newSketch(context, id + "F62", { "sketchPlane" : qUnion([Q0])});
            skCircle(sketch, "E182", {"center": v(672.09, 23) * mm, "radius": 1.5 * mm});
            skCircle(sketch, "E183", {"center": v(672.09, -23) * mm, "radius": 1.5 * mm});
            skCircle(sketch, "E184", {"center": v(639.09, 23) * mm, "radius": 1.5 * mm});
            skCircle(sketch, "E185", {"center": v(639.09, -23) * mm, "radius": 1.5 * mm});
            skCircle(sketch, "E186", {"center": v(655.59, 0) * mm, "radius": 3 * mm});
            skSolve(sketch);
        }
        {
            var Q0;
            Q0 = qSketchRegion(id + "F62", true);
            extrude(context, id + "F63", {"entities" : qUnion([Q0]), "operationType" : NewBodyOperationType.REMOVE, "oppositeDirection" : true, "depth" : 4 * mm});
        }
        {
            var Q0;
            Q0=qCreatedBy(makeId("Top.planeOp"),FACE);
            var sketch = newSketch(context, id + "F64", { "sketchPlane" : qUnion([Q0])});
            skLineSegment(sketch, "E187.bottom", {"start": v(1142.7, -62.5) * mm, "end": v(1267.7, -62.5) * mm});
            skLineSegment(sketch, "E187.top", {"start": v(1142.7, 62.5) * mm, "end": v(1267.7, 62.5) * mm});
            skLineSegment(sketch, "E187.left", {"start": v(1142.7, -62.5) * mm, "end": v(1142.7, 62.5) * mm});
            skLineSegment(sketch, "E187.right", {"start": v(1267.7, -62.5) * mm, "end": v(1267.7, 62.5) * mm});
            skPoint(sketch, "E187.middle", {"position": v(1205.2, 0) * mm});
            skSolve(sketch);
        }
        {
            var Q0;
            Q0 = qSketchRegion(id + "F64", true);
            extrude(context, id + "F65", {"entities" : qUnion([Q0]), "depth" : 4 * mm});
        }
        {
            var Q0;
            Q0=qCreatedBy(makeId("Front.planeOp"),FACE);
            var sketch = newSketch(context, id + "F66", { "sketchPlane" : qUnion([Q0])});
            skLineSegment(sketch, "E188", {"start": v(1310, 0) * mm, "end": v(1316, 0) * mm});
            skLineSegment(sketch, "E189", {"start": v(1316, 0) * mm, "end": v(1316, 5) * mm});
            skLineSegment(sketch, "E190", {"start": v(1316, 5) * mm, "end": v(1313, 5) * mm});
            skLineSegment(sketch, "E191", {"start": v(1313, 5) * mm, "end": v(1313, 50) * mm});
            skLineSegment(sketch, "E192", {"start": v(1313, 50) * mm, "end": v(1310, 50) * mm});
            skLineSegment(sketch, "E193", {"start": v(1310, 50) * mm, "end": v(1310, 0) * mm});
            skSolve(sketch);
        }
        {
            var Q0;
            Q0=qCreatedBy(makeId("Front.planeOp"),FACE);
            var sketch = newSketch(context, id + "F67", { "sketchPlane" : qUnion([Q0])});
            skLineSegment(sketch, "E194", {"start": v(1310, 54.37) * mm, "end": v(1310, -5.63) * mm, "construction": true});
            skSolve(sketch);
        }
        {
            var Q0;
            Q0 = qSketchRegion(id + "F66", true);
            var Q1;
            Q1 = qConstructionFilter(qBodyType(qCreatedBy(id + "F66" ,EDGE), BodyType.WIRE), ConstructionObject.NO);
            var Q2;
            Q2=sQuery(id+"F67.wireOp",EDGE,"E194");
            revolve(context, id + "F68", {"entities" : qUnion([Q0]), "surfaceEntities" : qUnion([Q1]), "axis" : qUnion([Q2]), "revolveType" : RevolveType.FULL});
        }
        {
            var Q0;
            Q0=makeQuery(id+"F65.opExtrude","CAP_FACE",FACE,{"disambiguationData":[OSD([sQuery(id+"F64.wireOp",EDGE,"E187.bottom"),sQuery(id+"F64.wireOp",EDGE,"E187.top"),sQuery(id+"F64.wireOp",EDGE,"E187.left"),sQuery(id+"F64.wireOp",EDGE,"E187.right")])],"isStart":true});
            var sketch = newSketch(context, id + "F69", { "sketchPlane" : qUnion([Q0])});
            skCircle(sketch, "E195", {"center": v(1172.7, 32.5) * mm, "radius": 5 * mm});
            skLineSegment(sketch, "E196.bottom", {"start": v(1232.7, 25) * mm, "end": v(1242.7, 25) * mm});
            skLineSegment(sketch, "E196.top", {"start": v(1232.7, 40) * mm, "end": v(1242.7, 40) * mm});
            skLineSegment(sketch, "E196.left", {"start": v(1232.7, 25) * mm, "end": v(1232.7, 40) * mm});
            skLineSegment(sketch, "E196.right", {"start": v(1242.7, 25) * mm, "end": v(1242.7, 40) * mm});
            skPoint(sketch, "E196.middle", {"position": v(1237.7, 32.5) * mm});
            skCircle(sketch, "E197", {"center": v(1205.2, 0) * mm, "radius": 3.5 * mm});
            skPoint(sketch, "E197.centerSnap0", {"position": v(1142.7, 0) * mm});
            skPoint(sketch, "E197.centerSnap1", {"position": v(1205.2, -62.5) * mm});
            skSolve(sketch);
        }
        {
            var Q0;
            Q0 = qSketchRegion(id + "F69", true);
            extrude(context, id + "F70", {"entities" : qUnion([Q0]), "operationType" : NewBodyOperationType.REMOVE, "oppositeDirection" : true, "depth" : 4 * mm});
        }
        {
            var Q0;
            Q0=qCreatedBy(makeId("Front.planeOp"),FACE);
            var sketch = newSketch(context, id + "F71", { "sketchPlane" : qUnion([Q0])});
            skLineSegment(sketch, "E198", {"start": v(1342.5, 0) * mm, "end": v(1345, 0) * mm});
            skLineSegment(sketch, "E199", {"start": v(1340, 11) * mm, "end": v(1340, 1.5) * mm});
            skLineSegment(sketch, "E200", {"start": v(1340, 1.5) * mm, "end": v(1340.5, 1.5) * mm});
            skLineSegment(sketch, "E201", {"start": v(1340.5, 1.5) * mm, "end": v(1340.5, 6.5) * mm});
            skLineSegment(sketch, "E202", {"start": v(1340.5, 6.5) * mm, "end": v(1342.5, 6.5) * mm});
            skLineSegment(sketch, "E203", {"start": v(1342.5, 6.5) * mm, "end": v(1342.5, 0) * mm});
            skLineSegment(sketch, "E204", {"start": v(1340, 11) * mm, "end": v(1345, 11) * mm});
            skLineSegment(sketch, "E205", {"start": v(1345, 11) * mm, "end": v(1345, 2) * mm});
            skLineSegment(sketch, "E206", {"start": v(1345, 2) * mm, "end": v(1347, 2) * mm});
            skLineSegment(sketch, "E207", {"start": v(1347, 2) * mm, "end": v(1347, 0) * mm});
            skLineSegment(sketch, "E208", {"start": v(1347, 0) * mm, "end": v(1345, 0) * mm});
            skSolve(sketch);
        }
        {
            var Q0;
            Q0=qCreatedBy(makeId("Front.planeOp"),FACE);
            var sketch = newSketch(context, id + "F72", { "sketchPlane" : qUnion([Q0])});
            skLineSegment(sketch, "E209", {"start": v(1340, 12.89) * mm, "end": v(1340, -2.11) * mm, "construction": true});
            skSolve(sketch);
        }
        {
            var Q0;
            Q0 = qSketchRegion(id + "F71", true);
            var Q1;
            Q1=sQuery(id+"F72.wireOp",EDGE,"E209");
            revolve(context, id + "F73", {"entities" : qUnion([Q0]), "axis" : qUnion([Q1]), "revolveType" : RevolveType.FULL});
        }
        {
            var Q0;
            Q0=qCreatedBy(makeId("Top.planeOp"),FACE);
            var sketch = newSketch(context, id + "F74", { "sketchPlane" : qUnion([Q0])});
            skLineSegment(sketch, "E210.bottom", {"start": v(1366.24, -9.5) * mm, "end": v(1380.24, -9.5) * mm});
            skLineSegment(sketch, "E210.top", {"start": v(1366.24, 9.5) * mm, "end": v(1380.24, 9.5) * mm});
            skLineSegment(sketch, "E210.left", {"start": v(1366.24, -9.5) * mm, "end": v(1366.24, 9.5) * mm});
            skLineSegment(sketch, "E210.right", {"start": v(1380.24, -9.5) * mm, "end": v(1380.24, 9.5) * mm});
            skPoint(sketch, "E210.middle", {"position": v(1373.24, 0) * mm});
            skSolve(sketch);
        }
        {
            var Q0;
            Q0 = qSketchRegion(id + "F74", true);
            extrude(context, id + "F75", {"entities" : qUnion([Q0]), "depth" : 15 * mm});
        }
        {
            var Q0;
            Q0=makeQuery(id+"F75.opExtrude","CAP_FACE",FACE,{"disambiguationData":[OSD([sQuery(id+"F74.wireOp",EDGE,"E210.bottom"),sQuery(id+"F74.wireOp",EDGE,"E210.top"),sQuery(id+"F74.wireOp",EDGE,"E210.left"),sQuery(id+"F74.wireOp",EDGE,"E210.right")])],"isStart":false});
            var sketch = newSketch(context, id + "F76", { "sketchPlane" : qUnion([Q0])});
            skLineSegment(sketch, "E211.bottom", {"start": v(1368.24, -7.5) * mm, "end": v(1378.24, -7.5) * mm});
            skLineSegment(sketch, "E211.top", {"start": v(1368.24, 7.5) * mm, "end": v(1378.24, 7.5) * mm});
            skLineSegment(sketch, "E211.left", {"start": v(1368.24, -7.5) * mm, "end": v(1368.24, 7.5) * mm});
            skLineSegment(sketch, "E211.right", {"start": v(1378.24, -7.5) * mm, "end": v(1378.24, 7.5) * mm});
            skPoint(sketch, "E211.middle", {"position": v(1373.24, 0) * mm});
            skPoint(sketch, "E211.middle.positionSnap0", {"position": v(1373.24, 9.5) * mm});
            skPoint(sketch, "E211.centerSnap0", {"position": v(1373.24, 9.5) * mm});
            skLineSegment(sketch, "E212.bottom", {"start": v(1366.24, -9.5) * mm, "end": v(1380.24, -9.5) * mm});
            skLineSegment(sketch, "E212.top", {"start": v(1366.24, 9.5) * mm, "end": v(1380.24, 9.5) * mm});
            skLineSegment(sketch, "E212.left", {"start": v(1366.24, -9.5) * mm, "end": v(1366.24, 9.5) * mm});
            skLineSegment(sketch, "E212.right", {"start": v(1380.24, -9.5) * mm, "end": v(1380.24, 9.5) * mm});
            skSolve(sketch);
        }
        {
            var Q0;
            Q0 = qSketchRegion(id + "F76", true);
            extrude(context, id + "F77", {"entities" : qUnion([Q0]), "operationType" : NewBodyOperationType.REMOVE, "oppositeDirection" : true, "depth" : 10 * mm});
        }
        {
            var Q0;
            Q0=makeQuery(id+"F75.opExtrude","CAP_FACE",FACE,{"disambiguationData":[OSD([sQuery(id+"F74.wireOp",EDGE,"E210.bottom"),sQuery(id+"F74.wireOp",EDGE,"E210.top"),sQuery(id+"F74.wireOp",EDGE,"E210.left"),sQuery(id+"F74.wireOp",EDGE,"E210.right")])],"isStart":true});
            var sketch = newSketch(context, id + "F78", { "sketchPlane" : qUnion([Q0])});
            skLineSegment(sketch, "E213.bottom", {"start": v(1369.24, -6) * mm, "end": v(1377.24, -6) * mm});
            skLineSegment(sketch, "E213.top", {"start": v(1369.24, 6) * mm, "end": v(1377.24, 6) * mm});
            skLineSegment(sketch, "E213.left", {"start": v(1369.24, -6) * mm, "end": v(1369.24, 6) * mm});
            skLineSegment(sketch, "E213.right", {"start": v(1377.24, -6) * mm, "end": v(1377.24, 6) * mm});
            skPoint(sketch, "E213.middle", {"position": v(1373.24, 0) * mm});
            skPoint(sketch, "E213.middle.positionSnap0", {"position": v(1373.24, 9.5) * mm});
            skPoint(sketch, "E213.centerSnap0", {"position": v(1373.24, 9.5) * mm});
            skLineSegment(sketch, "E214.bottom", {"start": v(1366.24, -9.5) * mm, "end": v(1380.24, -9.5) * mm});
            skLineSegment(sketch, "E214.top", {"start": v(1366.24, 9.5) * mm, "end": v(1380.24, 9.5) * mm});
            skLineSegment(sketch, "E214.left", {"start": v(1366.24, -9.5) * mm, "end": v(1366.24, 9.5) * mm});
            skLineSegment(sketch, "E214.right", {"start": v(1380.24, -9.5) * mm, "end": v(1380.24, 9.5) * mm});
            skSolve(sketch);
        }
        {
            var Q0;
            Q0 = qSketchRegion(id + "F78", true);
            extrude(context, id + "F79", {"entities" : qUnion([Q0]), "operationType" : NewBodyOperationType.REMOVE, "oppositeDirection" : true, "depth" : 3 * mm});
        }
        {
            var Q0;
            Q0=makeQuery(id+"F79.boolean.opBoolean","COPY",FACE,{"derivedFrom":makeQuery(id+"F79.opExtrude","SWEPT_FACE",FACE,{"disambiguationData":[OSD([sQuery(id+"F78.wireOp",EDGE,"E213.right")])]})});
            var sketch = newSketch(context, id + "F80", { "sketchPlane" : qUnion([Q0])});
            skLineSegment(sketch, "E215", {"start": v(-6, 0) * mm, "end": v(-6, 2.25) * mm});
            skLineSegment(sketch, "E216", {"start": v(-6, 0) * mm, "end": v(6, 0) * mm});
            skLineSegment(sketch, "E217", {"start": v(6, 0) * mm, "end": v(6, 1) * mm});
            skArc(sketch, "E218", {"start": v(6, 1) * mm, "mid": v(0.1, 2.58) * mm, "end": v(-6, 2.25) * mm});
            skSolve(sketch);
        }
        {
            var Q0;
            Q0 = qSketchRegion(id + "F80", true);
            extrude(context, id + "F81", {"entities" : qUnion([Q0]), "operationType" : NewBodyOperationType.REMOVE, "oppositeDirection" : true, "depth" : 8 * mm});
        }
        {
            var Q0;
            Q0=qCreatedBy(makeId("Front.planeOp"),FACE);
            var sketch = newSketch(context, id + "F82", { "sketchPlane" : qUnion([Q0])});
            skLineSegment(sketch, "E219", {"start": v(1400, 0) * mm, "end": v(1410, 0) * mm});
            skLineSegment(sketch, "E220", {"start": v(1410, 0) * mm, "end": v(1411, 4) * mm});
            skLineSegment(sketch, "E221", {"start": v(1411, 4) * mm, "end": v(1403, 4) * mm});
            skLineSegment(sketch, "E222", {"start": v(1403, 4) * mm, "end": v(1403, 1.57) * mm});
            skLineSegment(sketch, "E223", {"start": v(1403, 1.57) * mm, "end": v(1400, 1.57) * mm});
            skLineSegment(sketch, "E224", {"start": v(1400, 1.57) * mm, "end": v(1400, 0) * mm});
            skSolve(sketch);
        }
        {
            var Q0;
            Q0=qCreatedBy(makeId("Front.planeOp"),FACE);
            var sketch = newSketch(context, id + "F83", { "sketchPlane" : qUnion([Q0])});
            skLineSegment(sketch, "E225", {"start": v(1400, 6.8) * mm, "end": v(1400, -3.2) * mm, "construction": true});
            skSolve(sketch);
        }
        {
            var Q0;
            Q0 = qSketchRegion(id + "F82", true);
            var Q1;
            Q1=sQuery(id+"F83.wireOp",EDGE,"E225");
            var Q2;
            Q2=sQuery(id+"F83.wireOp",EDGE,"E225");
            revolve(context, id + "F84", {"entities" : qUnion([Q0]), "surfaceEntities" : qUnion([Q1]), "axis" : qUnion([Q2]), "revolveType" : RevolveType.FULL});
        }
        {
            var Q0;
            Q0=makeQuery(id+"F84.opRevolve","SWEPT_FACE",FACE,{"disambiguationData":[OSD([sQuery(id+"F82.wireOp",EDGE,"E219")])]});
            var sketch = newSketch(context, id + "F85", { "sketchPlane" : qUnion([Q0])});
            skLineSegment(sketch, "E226.bottom", {"start": v(1390.04, 0.89) * mm, "end": v(1394.04, 0.89) * mm});
            skLineSegment(sketch, "E226.top", {"start": v(1390.04, -0.11) * mm, "end": v(1394.04, -0.11) * mm});
            skLineSegment(sketch, "E226.left", {"start": v(1390.04, 0.89) * mm, "end": v(1390.04, -0.11) * mm});
            skLineSegment(sketch, "E226.right", {"start": v(1394.04, 0.89) * mm, "end": v(1394.04, -0.11) * mm});
            skSolve(sketch);
        }
        {
            var Q0;
            Q0 = qSketchRegion(id + "F85", true);
            extrude(context, id + "F86", {"entities" : qUnion([Q0]), "operationType" : NewBodyOperationType.REMOVE, "oppositeDirection" : true, "depth" : 0.5 * mm});
        }
        {
            var Q0;
            Q0=qCreatedBy(makeId("Front.planeOp"),FACE);
            var sketch = newSketch(context, id + "F87", { "sketchPlane" : qUnion([Q0])});
            skLineSegment(sketch, "E227", {"start": v(-1300, 199.19) * mm, "end": v(-1300, -50.81) * mm, "construction": true});
            skSolve(sketch);
        }
        {
            var Q0;
            Q0=qCreatedBy(makeId("Front.planeOp"),FACE);
            var sketch = newSketch(context, id + "F88", { "sketchPlane" : qUnion([Q0])});
            skArc(sketch, "E228", {"start": v(-1275, 0) * mm, "mid": v(-1220.23, 30.84) * mm, "end": v(-1199, 90) * mm});
            skLineSegment(sketch, "E229", {"start": v(-1275, 0) * mm, "end": v(-1300, 0) * mm});
            skLineSegment(sketch, "E230", {"start": v(-1300, 0) * mm, "end": v(-1300, 1) * mm});
            skLineSegment(sketch, "E231", {"start": v(-1300, 1) * mm, "end": v(-1275, 1) * mm});
            skArc(sketch, "E232", {"start": v(-1275, 1) * mm, "mid": v(-1220.94, 31.54) * mm, "end": v(-1200, 90) * mm});
            skLineSegment(sketch, "E233", {"start": v(-1200, 90) * mm, "end": v(-1199, 90) * mm});
            skSolve(sketch);
        }
        {
            var Q0;
            Q0 = qSketchRegion(id + "F88", true);
            var Q1;
            Q1=sQuery(id+"F87.wireOp",EDGE,"E227");
            revolve(context, id + "F89", {"entities" : qUnion([Q0]), "axis" : qUnion([Q1]), "revolveType" : RevolveType.FULL});
        }
        {
            var Q0;
            Q0=qCreatedBy(makeId("Top.planeOp"),FACE);
            var sketch = newSketch(context, id + "F90", { "sketchPlane" : qUnion([Q0])});
            skCircle(sketch, "E234", {"center": v(-1600, 0) * mm, "radius": 97.5 * mm});
            skSolve(sketch);
        }
        {
            var Q0;
            Q0 = qSketchRegion(id + "F90", true);
            extrude(context, id + "F91", {"entities" : qUnion([Q0]), "depth" : 4 * mm, "offsetDistance" : 25 * mm});
        }
        {
            var Q0;
            Q0=makeQuery(id+"F91.opExtrude","CAP_FACE",FACE,{"disambiguationData":[OSD([sQuery(id+"F90.wireOp",EDGE,"E234")])],"isStart":false});
            var sketch = newSketch(context, id + "F92", { "sketchPlane" : qUnion([Q0])});
            skCircle(sketch, "E235.cCircle", {"center": v(-1600, 0) * mm, "radius": 92.5 * mm, "construction": true});
            skLineSegment(sketch, "E235.0", {"start": v(-1680.1, -46.25) * mm, "end": v(-1600, 92.5) * mm, "construction": true});
            skLineSegment(sketch, "E235.1", {"start": v(-1600, 92.5) * mm, "end": v(-1519.9, -46.25) * mm, "construction": true});
            skLineSegment(sketch, "E235.2", {"start": v(-1519.9, -46.25) * mm, "end": v(-1680.1, -46.25) * mm, "construction": true});
            skCircle(sketch, "E236", {"center": v(-1600, 92.5) * mm, "radius": 2 * mm});
            skCircle(sketch, "E237", {"center": v(-1680.1, -46.25) * mm, "radius": 2 * mm});
            skCircle(sketch, "E238", {"center": v(-1519.9, -46.25) * mm, "radius": 2 * mm});
            skSolve(sketch);
        }
        {
            var Q0;
            Q0 = qSketchRegion(id + "F92", true);
            extrude(context, id + "F93", {"entities" : qUnion([Q0]), "operationType" : NewBodyOperationType.REMOVE, "oppositeDirection" : true, "depth" : 4 * mm, "offsetDistance" : 25 * mm});
        }
        {
            var Q0;
            Q0=qCreatedBy(makeId("Front.planeOp"),FACE);
            var sketch = newSketch(context, id + "F94", { "sketchPlane" : qUnion([Q0])});
            skLineSegment(sketch, "E239", {"start": v(-1128.18, 0) * mm, "end": v(-1128.18, 5) * mm});
            skLineSegment(sketch, "E240", {"start": v(-1128.18, 5) * mm, "end": v(-1134.18, 5) * mm});
            skLineSegment(sketch, "E241", {"start": v(-1134.18, 5) * mm, "end": v(-1134.18, 6) * mm});
            skLineSegment(sketch, "E242", {"start": v(-1134.18, 6) * mm, "end": v(-1127.18, 6) * mm});
            skLineSegment(sketch, "E243", {"start": v(-1127.18, 6) * mm, "end": v(-1127.18, 0) * mm});
            skLineSegment(sketch, "E244", {"start": v(-1127.18, 0) * mm, "end": v(-1128.18, 0) * mm});
            skSolve(sketch);
        }
        {
            var Q0;
            Q0 = qSketchRegion(id + "F94", true);
            extrude(context, id + "F95", {"entities" : qUnion([Q0]), "endBound" : BoundingType.SYMMETRIC, "depth" : 5 * mm, "offsetDistance" : 25 * mm});
        }
        {
            var Q0;
            Q0=makeQuery(id+"F95.opExtrude","SWEPT_FACE",FACE,{"disambiguationData":[OSD([sQuery(id+"F94.wireOp",EDGE,"E242")])]});
            var sketch = newSketch(context, id + "F96", { "sketchPlane" : qUnion([Q0])});
            skCircle(sketch, "E245", {"center": v(-1131.18, 0) * mm, "radius": 1.5 * mm});
            skSolve(sketch);
        }
        {
            var Q0;
            Q0 = qSketchRegion(id + "F96", true);
            extrude(context, id + "F97", {"entities" : qUnion([Q0]), "operationType" : NewBodyOperationType.REMOVE, "oppositeDirection" : true, "depth" : 1 * mm, "offsetDistance" : 25 * mm});
        }
        {
            var Q0;
            Q0=qCreatedBy(makeId("Front.planeOp"),FACE);
            var sketch = newSketch(context, id + "F98", { "sketchPlane" : qUnion([Q0])});
            skLineSegment(sketch, "E246", {"start": v(-2000, 137.4) * mm, "end": v(-2000, -62.6) * mm, "construction": true});
            skSolve(sketch);
        }
        {
            var Q0;
            Q0=qCreatedBy(makeId("Front.planeOp"),FACE);
            var sketch = newSketch(context, id + "F99", { "sketchPlane" : qUnion([Q0])});
            skCircle(sketch, "E247", {"center": v(-1960, 0) * mm, "radius": 7.5 * mm});
            skSolve(sketch);
        }
        {
            var Q0;
            Q0 = qSketchRegion(id + "F99", true);
            var Q1;
            Q1=sQuery(id+"F98.wireOp",EDGE,"E246");
            revolve(context, id + "F100", {"entities" : qUnion([Q0]), "axis" : qUnion([Q1]), "revolveType" : RevolveType.FULL});
        }
    });
